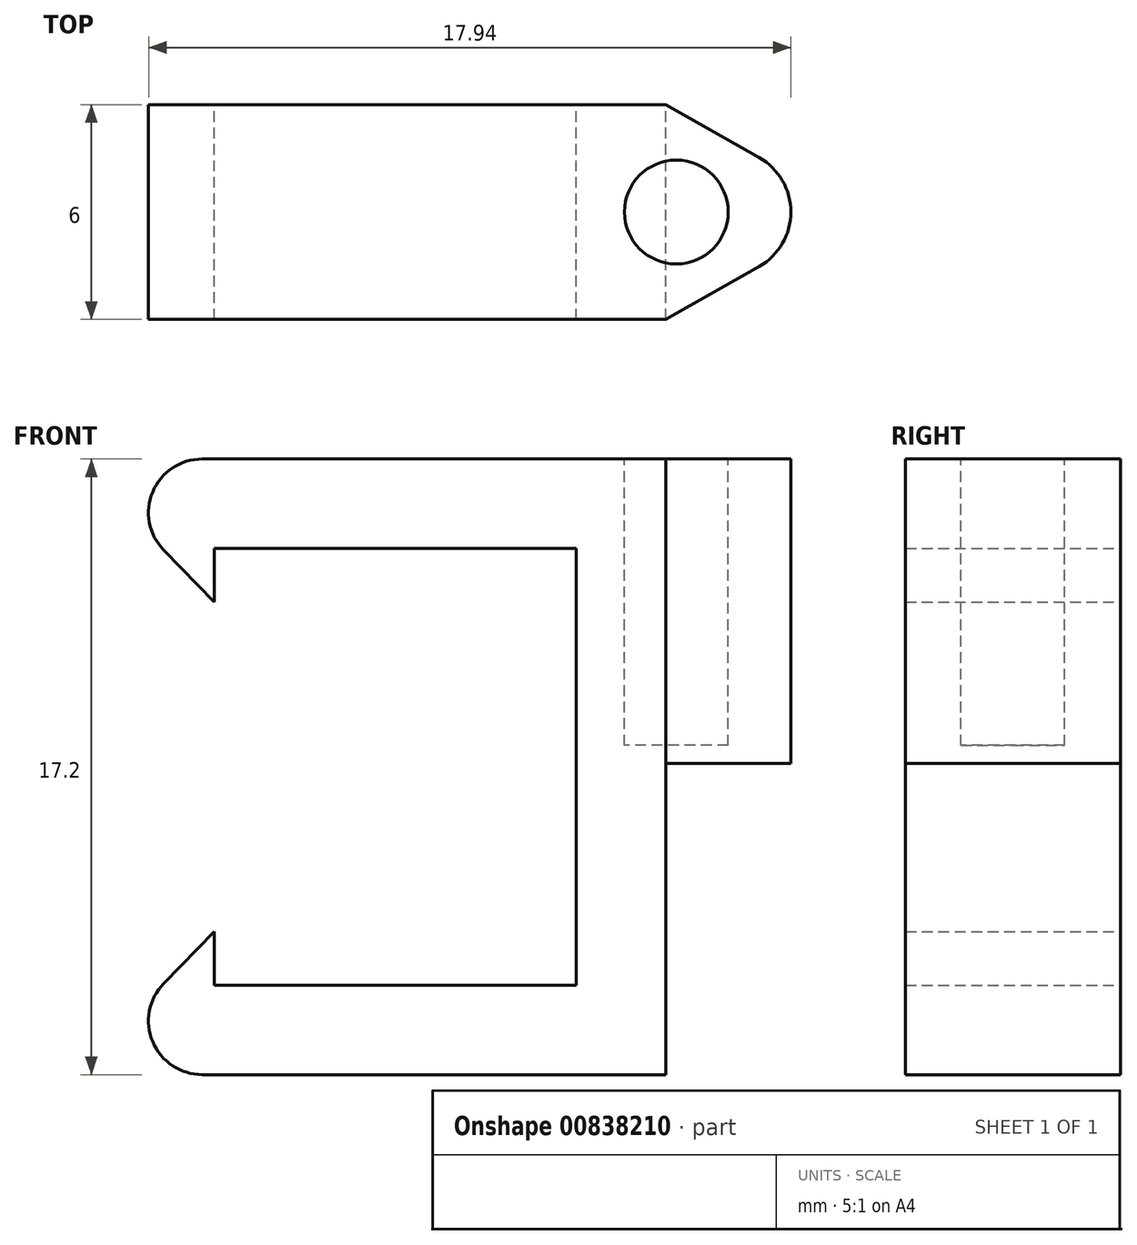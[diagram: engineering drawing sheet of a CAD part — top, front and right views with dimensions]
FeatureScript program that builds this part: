
annotation { "Feature Type Name" : "Feature", "Feature Type Description" : "" }
export const myFeature = defineFeature(function(context is Context, id is Id, definition is map)
    precondition{}
    {
        {
            var Q0;
            Q0=qCreatedBy(makeId("Front.planeOp"),FACE);
            var sketch = newSketch(context, id + "F0", { "sketchPlane" : qUnion([Q0])});
            skLineSegment(sketch, "E0.top", {"start": v(0, -12.2) * mm, "end": v(-10.1, -12.2) * mm});
            skLineSegment(sketch, "E0.left", {"start": v(0, 0) * mm, "end": v(0, -12.2) * mm, "construction": true});
            skLineSegment(sketch, "E1", {"start": v(-10.1, -10.7) * mm, "end": v(-14, -14.7) * mm});
            skLineSegment(sketch, "E2", {"start": v(-14, -14.7) * mm, "end": v(2.5, -14.7) * mm});
            skLineSegment(sketch, "E3", {"start": v(2.5, -14.7) * mm, "end": v(2.5, 0) * mm});
            skLineSegment(sketch, "E4", {"start": v(2.5, 0) * mm, "end": v(6, 0) * mm});
            skLineSegment(sketch, "E5", {"start": v(6, 0) * mm, "end": v(6, 2.5) * mm});
            skLineSegment(sketch, "E6", {"start": v(6, 2.5) * mm, "end": v(-14, 2.5) * mm});
            skLineSegment(sketch, "E7", {"start": v(-14, 2.5) * mm, "end": v(-10.1, -1.5) * mm});
            skLineSegment(sketch, "E8", {"start": v(0, 0) * mm, "end": v(0, -12.2) * mm});
            skLineSegment(sketch, "E9", {"start": v(-10.1, -12.2) * mm, "end": v(-10.1, -10.7) * mm});
            skLineSegment(sketch, "E10.trimOffspring", {"start": v(-10.1, -10.7) * mm, "end": v(-10.1, -12.2) * mm, "construction": true});
            skLineSegment(sketch, "E11", {"start": v(-10.1, -1.5) * mm, "end": v(-10.1, 0) * mm});
            skLineSegment(sketch, "E12", {"start": v(-10.1, 0) * mm, "end": v(0, 0) * mm});
            skLineSegment(sketch, "E13", {"start": v(0, 0) * mm, "end": v(0, 8.68) * mm, "construction": true});
            skLineSegment(sketch, "E14", {"start": v(0, -12.2) * mm, "end": v(0, -26.61) * mm, "construction": true});
            skSolve(sketch);
        }
        {
            var Q0;
            Q0 = qSketchRegion(id + "F0", true);
            extrude(context, id + "F1", {"entities" : qUnion([Q0]), "depth" : 6 * mm, "offsetDistance" : 25 * mm});
        }
        {
            var Q0;
            Q0=makeQuery(id+"F1.opExtrude","SWEPT_EDGE",EDGE,{"disambiguationData":[OSD([sQuery(id+"F0.wireOp",EDGE,"E1"),sQuery(id+"F0.wireOp",EDGE,"E2")])]});
            var Q1;
            Q1=makeQuery(id+"F1.opExtrude","SWEPT_EDGE",EDGE,{"disambiguationData":[OSD([sQuery(id+"F0.wireOp",EDGE,"E6"),sQuery(id+"F0.wireOp",EDGE,"E7")])]});
            fillet(context, id + "F2", {"entities" : qUnion([Q0, Q1]), "radius" : 1.5 * mm, "tangentPropagation" : true, "allowEdgeOverflow" : false});
        }
        {
            var Q0;
            Q0=makeQuery(id+"F1.opExtrude","SWEPT_FACE",FACE,{"disambiguationData":[OSD([sQuery(id+"F0.wireOp",EDGE,"E4")])]});
            var sketch = newSketch(context, id + "F3", { "sketchPlane" : qUnion([Q0])});
            skPoint(sketch, "E15.startSnap0", {"position": v(4.25, 6) * mm});
            skArc(sketch, "E16", {"start": v(5.11, 1.48) * mm, "mid": v(6, 3) * mm, "end": v(5.11, 4.52) * mm});
            skLineSegment(sketch, "E17", {"start": v(2.5, 6) * mm, "end": v(5.11, 4.52) * mm});
            skLineSegment(sketch, "E18", {"start": v(2.5, 0) * mm, "end": v(5.11, 1.48) * mm});
            skPoint(sketch, "E19.orphan", {"position": v(2.5, 3) * mm});
            skPoint(sketch, "E20.start.orphan", {"position": v(6, 3) * mm});
            skPoint(sketch, "E21.trimOffspring.start.orphan", {"position": v(4.25, 3.63) * mm});
            skPoint(sketch, "E22.trimOffspring.end.orphan", {"position": v(4.25, 0) * mm});
            skSolve(sketch);
        }
        {
            var Q0;
            Q0 = qSketchRegion(id + "F3", true);
            var Q1;
            {var subQ1=sQuery(id+"F3.wireOp",EDGE,"E17");Q1=makeQuery(id+"F3.imprint","IMPRINT",FACE,{"disambiguationData":[TD([[makeQuery(id+"F3.imprint","IMPRINT",EDGE,{"derivedFrom":subQ1}),-1.0]])]});}
            extrude(context, id + "F4", {"entities" : qUnion([Q0, Q1]), "operationType" : NewBodyOperationType.ADD, "depth" : 6 * mm, "offsetDistance" : 25 * mm});
        }
        {
            var Q0;
            Q0 = qSketchRegion(id + "F3", true);
            var Q1;
            {var subQ1=sQuery(id+"F0.wireOp",EDGE,"E4");var subQ2=makeQuery(id+"F1.opExtrude","SWEPT_FACE",FACE,{"disambiguationData":[OSD([subQ1])]});Q1=makeQuery(id+"F4.boolean.opBoolean","SPLIT",FACE,{"disambiguationData":[TD([makeQuery(id+"F4.opExtrude","SWEPT_FACE",FACE,{"disambiguationData":[OSD([sQuery(id+"F3.wireOp",EDGE,"E18")])]})])],"derivedFrom":subQ2});}
            var Q2;
            {var subQ0=sQuery(id+"F0.wireOp",EDGE,"E4");var subQ1=makeQuery(id+"F1.opExtrude","SWEPT_FACE",FACE,{"disambiguationData":[OSD([subQ0])]});Q2=makeQuery(id+"F4.boolean.opBoolean","SPLIT",FACE,{"disambiguationData":[TD([makeQuery(id+"F4.opExtrude","SWEPT_FACE",FACE,{"disambiguationData":[OSD([sQuery(id+"F3.wireOp",EDGE,"E17")])]})])],"derivedFrom":subQ1});}
            extrude(context, id + "F5", {"entities" : qUnion([Q0, Q1, Q2]), "operationType" : NewBodyOperationType.REMOVE, "oppositeDirection" : true, "depth" : 4 * mm, "offsetDistance" : 25 * mm});
        }
        {
            var Q0;
            Q0=makeQuery(id+"F1.opExtrude","SWEPT_FACE",FACE,{"disambiguationData":[OSD([sQuery(id+"F0.wireOp",EDGE,"E6")])]});
            var sketch = newSketch(context, id + "F6", { "sketchPlane" : qUnion([Q0])});
            skLineSegment(sketch, "E23", {"start": v(0, 0) * mm, "end": v(0, -6) * mm, "construction": true});
            skLineSegment(sketch, "E24", {"start": v(0, -3) * mm, "end": v(8.7, -3) * mm, "construction": true});
            skCircle(sketch, "E25", {"center": v(2.8, -3) * mm, "radius": 1.45 * mm});
            skSolve(sketch);
        }
        {
            var Q0;
            Q0=makeQuery(id+"F6.imprint","IMPRINT",FACE,{"disambiguationData":[TD([[makeQuery(id+"F6.imprint","IMPRINT",EDGE,{"derivedFrom":sQuery(id+"F6.wireOp",EDGE,"E25")}),1.0]])]});
            extrude(context, id + "F7", {"entities" : qUnion([Q0]), "operationType" : NewBodyOperationType.REMOVE, "oppositeDirection" : true, "depth" : 8 * mm, "offsetDistance" : 25 * mm});
        }
    });
